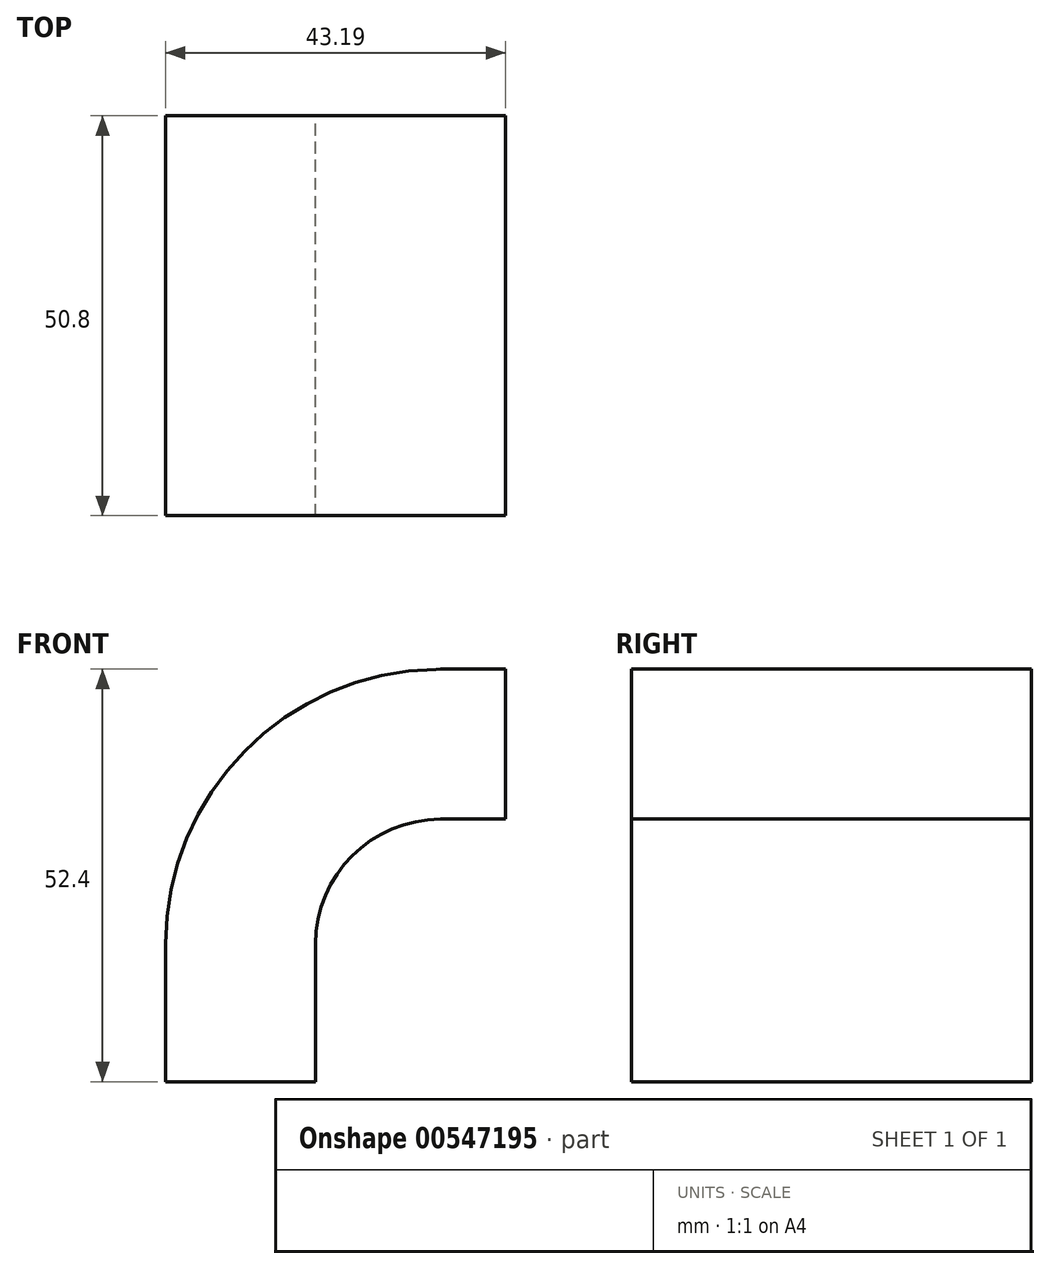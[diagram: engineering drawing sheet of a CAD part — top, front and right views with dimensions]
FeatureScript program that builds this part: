
annotation { "Feature Type Name" : "Feature", "Feature Type Description" : "" }
export const myFeature = defineFeature(function(context is Context, id is Id, definition is map)
    precondition{}
    {
        {
            var Q0;
            Q0=qCreatedBy(makeId("Front.planeOp"),FACE);
            var sketch = newSketch(context, id + "F0", { "sketchPlane" : qUnion([Q0])});
            skLineSegment(sketch, "E0.bottom", {"start": v(41.28, -9.52) * mm, "end": v(-41.28, -9.53) * mm});
            skLineSegment(sketch, "E0.top", {"start": v(41.28, 9.53) * mm, "end": v(-41.28, 9.53) * mm});
            skLineSegment(sketch, "E0.left", {"start": v(41.28, -9.52) * mm, "end": v(41.28, 9.53) * mm});
            skLineSegment(sketch, "E0.right", {"start": v(-41.28, -9.53) * mm, "end": v(-41.28, 9.53) * mm});
            skPoint(sketch, "E0.middle", {"position": v(0, 0) * mm});
            skLineSegment(sketch, "E1.bottom", {"start": v(65.4, 38.1) * mm, "end": v(116.2, 38.1) * mm});
            skLineSegment(sketch, "E1.top", {"start": v(65.4, 66.68) * mm, "end": v(116.2, 66.68) * mm});
            skLineSegment(sketch, "E1.left", {"start": v(65.4, 38.1) * mm, "end": v(65.4, 66.68) * mm});
            skLineSegment(sketch, "E1.right", {"start": v(116.2, 38.1) * mm, "end": v(116.2, 66.68) * mm});
            skPoint(sketch, "E1.middle", {"position": v(90.8, 52.39) * mm});
            skLineSegment(sketch, "E2", {"start": v(41.28, 9.53) * mm, "end": v(41.28, 27) * mm});
            skArc(sketch, "E3", {"start": v(41.27, 27) * mm, "mid": v(45.92, 38.23) * mm, "end": v(57.15, 42.88) * mm});
            skLineSegment(sketch, "E4", {"start": v(57.15, 42.88) * mm, "end": v(90.8, 42.88) * mm});
            skLineSegment(sketch, "E5.0", {"start": v(57.15, 61.93) * mm, "end": v(90.8, 61.93) * mm});
            skArc(sketch, "E5.1", {"start": v(22.23, 27) * mm, "mid": v(32.45, 51.7) * mm, "end": v(57.15, 61.93) * mm});
            skLineSegment(sketch, "E5.2", {"start": v(22.22, 9.53) * mm, "end": v(22.22, 27) * mm});
            skLineSegment(sketch, "E6", {"start": v(90.8, 38.1) * mm, "end": v(90.8, 66.68) * mm});
            skFitSpline(sketch, "E7", {"points": [v(-41.28, 9.53) * mm, v(57.15, 61.93) * mm], "startDerivative": vector(0.74, 86.82) * mm, "endDerivative": vector(171.45, 1.15) * mm});
            skSolve(sketch);
        }
        {
            var Q0;
            {var subQ1=sQuery(id+"F0.wireOp",EDGE,"E2");Q0=makeQuery(id+"F0.imprint","IMPRINT",FACE,{"disambiguationData":[TD([[makeQuery(id+"F0.imprint","IMPRINT",EDGE,{"derivedFrom":subQ1}),1.0]])]});}
            extrude(context, id + "F1", {"entities" : qUnion([Q0]), "endBound" : BoundingType.SYMMETRIC, "depth" : 50.8 * mm, "offsetDistance" : 25.4 * mm});
        }
    });
